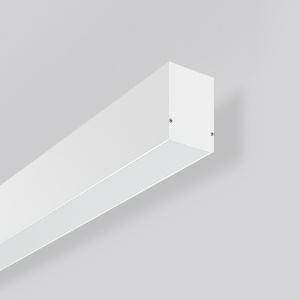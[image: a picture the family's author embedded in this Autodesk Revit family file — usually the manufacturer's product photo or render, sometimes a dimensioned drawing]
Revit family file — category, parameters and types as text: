
# Revit family: less_is_more_50_312613_002_1_7ac3
name_source: partatom
category: Lighting Fixtures
units: mm (PartAtom-declared; Revit-internal decimal feet)

## family parameters
Cut with Voids When Loaded = No
Host = Face
Light Source = No
Part Type = Normal
Room Calculation Point = No
Round Connector Dimension = Use Diameter
Shared = No

## types (1)
- LESS IS MORE 50 (1 x LED Modul 840, 2650 lm, 4000)
    Apparent Load = 20 VA
    CIE Flux Codes = 48 80 96 100 100
    Color Rendering = 80
    Color Temperature = 4000
    Default Elevation = 1800 mm
    Description = Series: LESS IS MORE 50
Linear wall luminaires. Housing: extruded aluminium profile, powder-coated. End cap aluminium powder-coated. Diffuser made of non-yellowing plastic (PMMA), opal. Direct light emission. Suitable for Wall (surface). LED unit with integrated converter interchangeable and removable. Suitable for through-wiring. With sensors or as a safety luminaire on request. 
Colour: traffic white, matt (RAL 9016)
Length: 1967 mm
Width: 67 mm
Height: 75 mm
Lamp: LED
Socket: without socket
Colour temperature: 4000K
Colour rendering index (CRI): 80
System power: 20 W
Rated luminous flux: 2650 lm
Luminous efficiency: 133 lm/W
Control gear: Regulated power supply
Protection class: I
Type of protection: IP 20
    Height = 75 mm
    Lamp = 1 x LED Modul 840
    Lamp Light Flux = 2650 lm
    Lamp count = 1
    Length = 1967 mm
    Lifetime = 50000 h
    Luminous efficacy = 133 lm/W
    Manufacturer = RZB
    ModVariant = No
    Model = 312613.002.1
    Mounting Place = Wall
    Mounting Type = Surface mounted
    Number of Poles = 1
    OnlyDefault = Yes
    Power Factor = 1
    Product Name = LESS IS MORE 50
    Product group = Surface mounted LED linear luminaires
    ProductGroupID = 2007
    Protection Class = Protection class I
    Protection Degree = IP 20
    RLX_Detail_Level = 1
    RLX_Emergency_Light_Flux = 0 lm
    RLX_Emergency_Type = 0
    RLX_Emergency_Type_DB = No
    RlxData = <blob elided: 35161 chars, md5=2325af82>
    Socket = socket
    Standby Power = 0 W
    System Light Flux = 2650 lm
    System Power = 20 W
    Type Comments = Product without accessories
    Type Image = 312606.002.jpg
    URL = http://relux.com
    VarID = ---
    Voltage = 0 V
    Weight = 0.00 kg
    Width = 67 mm

## geometry (parser evidence)
native form markers: Blend x4, Sweep x9
no freeform markers — native parametric forms only
